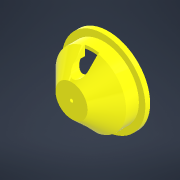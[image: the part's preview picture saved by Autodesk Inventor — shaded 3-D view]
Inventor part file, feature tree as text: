
AUTODESK INVENTOR PART (.ipt)
format: ipt  version: 2022 (Build 260153000, 153)  size: 190,464 bytes
history: native  units: mm
features: sketch x3, revolve x1, hole x1, plane x1, extrude x1, pattern_circular x1
ambient origin geometry x8: Origin, YZ Plane, XZ Plane, XY Plane, X Axis, Y Axis, Z Axis, Center Point
bodies: Solid1 (feature_tree)
feature tree (8):
  revolve  "Revolution1"  [1 undecoded]
  hole  "Hole2"  [1 undecoded]
  plane  "Work Plane2"
  extrude  "Extrusion1"  Depth=10.0mm
  pattern_circular  "Circular Pattern2"  [2 undecoded]
  sketch  "Sketch1"  dims[d3=26.0mm d5=20.0mm]
  sketch  "Sketch4"  dims[d6=1.0mm d7=135.0deg]
  sketch  "Sketch5"  dims[d8=1.0mm d9=10.0mm d10=11.5mm d11=1.5mm d12=360.0deg d24=16.0mm d25=6.0mm d26=17.3mm d27=2.0mm d28=90.0deg d29=1.4mm d30=20.594885mm d32=1.0mm d33=1.0mm d34=0.5mm d35=30.0deg d36=0.0mm d37=4.5mm d38=6.0mm d39=10.0mm d40=0.0mm d41=20.0mm d42=360.0deg d31=1.0mm]
note: 4 required parameter values undecoded (feature->parameter linkage not recoverable at this tier; creation-order binding heuristic only, values carry confidence <= 0.55)